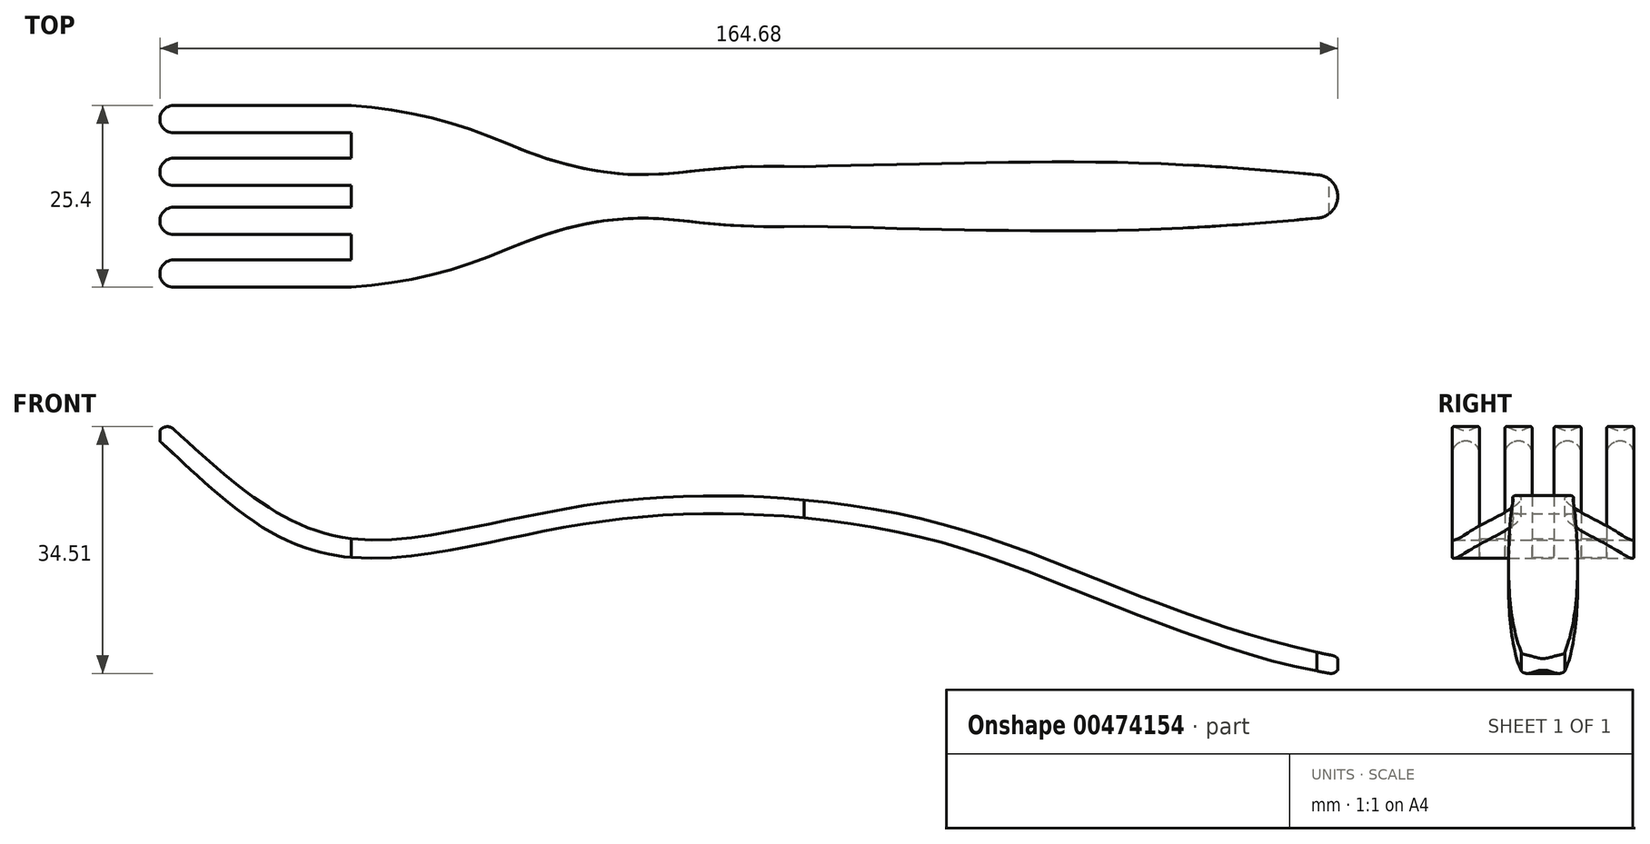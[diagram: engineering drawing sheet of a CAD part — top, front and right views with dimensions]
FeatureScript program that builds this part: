
annotation { "Feature Type Name" : "Feature", "Feature Type Description" : "" }
export const myFeature = defineFeature(function(context is Context, id is Id, definition is map)
    precondition{}
    {
        {
            var Q0;
            Q0=qCreatedBy(makeId("Front.planeOp"),FACE);
            var sketch = newSketch(context, id + "F0", { "sketchPlane" : qUnion([Q0])});
            skFitSpline(sketch, "E0", {"points": [v(0, 0) * mm, v(13.61, -11.16) * mm, v(28.58, -15.5) * mm, v(60.74, -10.24) * mm, v(97.9, -11.19) * mm, v(122.55, -18.4) * mm, v(162.04, -31.66) * mm], "startDerivative": vector(98.22, -90.14) * mm, "endDerivative": vector(217.26, -42.93) * mm});
            skFitSpline(sketch, "E1.0", {"points": [v(-1.72, -1.87) * mm, v(0.33, -3.75) * mm, v(4.54, -7.63) * mm, v(11.25, -12.95) * mm, v(17.27, -16.18) * mm, v(22.74, -17.67) * mm, v(26.46, -18.07) * mm, v(29.66, -18.05) * mm, v(32.14, -17.87) * mm, v(34.7, -17.57) * mm, v(38.22, -17.03) * mm, v(42.8, -16.14) * mm, v(48.55, -14.94) * mm, v(53.5, -13.95) * mm, v(57.51, -13.26) * mm, v(60.54, -12.8) * mm, v(63.59, -12.45) * mm, v(67.68, -12.09) * mm, v(72.82, -11.85) * mm, v(78.93, -11.86) * mm, v(84.9, -12.15) * mm, v(89.7, -12.6) * mm, v(93.36, -13.05) * mm, v(96.02, -13.44) * mm, v(98.57, -13.88) * mm, v(101.84, -14.5) * mm, v(105.73, -15.41) * mm, v(110.23, -16.69) * mm, v(114.74, -18.17) * mm, v(118.64, -19.6) * mm, v(121.92, -20.87) * mm, v(125.34, -22.22) * mm, v(129.84, -24.04) * mm, v(135.6, -26.3) * mm, v(141.68, -28.57) * mm, v(150.16, -31.43) * mm, v(156.9, -33.24) * mm, v(161.54, -34.16) * mm]});
            skArc(sketch, "E2", {"start": v(0, 0) * mm, "mid": v(-1.8, -0.08) * mm, "end": v(-1.72, -1.87) * mm});
            skArc(sketch, "E3", {"start": v(161.54, -34.16) * mm, "mid": v(163.03, -33.16) * mm, "end": v(162.04, -31.66) * mm});
            skSolve(sketch);
        }
        {
            var Q0;
            Q0 = qSketchRegion(id + "F0", true);
            extrude(context, id + "F1", {"entities" : qUnion([Q0]), "depth" : 25.4 * mm});
        }
        {
            var Q0;
            Q0=qCreatedBy(makeId("Top.planeOp"),FACE);
            var sketch = newSketch(context, id + "F2", { "sketchPlane" : qUnion([Q0])});
            skLineSegment(sketch, "E4.bottom", {"start": v(-6.25, 9.3) * mm, "end": v(172.92, 9.3) * mm});
            skLineSegment(sketch, "E4.top", {"start": v(-6.25, -34.7) * mm, "end": v(172.92, -34.7) * mm});
            skLineSegment(sketch, "E4.left", {"start": v(-6.25, 9.3) * mm, "end": v(-6.25, -34.7) * mm});
            skLineSegment(sketch, "E4.right", {"start": v(172.92, 9.3) * mm, "end": v(172.92, -34.7) * mm});
            skFitSpline(sketch, "E5", {"points": [v(0, 0) * mm, v(24.83, 0) * mm, v(41.72, -3.41) * mm, v(52.72, -7.58) * mm, v(65.82, -9.67) * mm, v(88.17, -8.53) * mm], "startDerivative": vector(74.86, 1.88) * mm, "endDerivative": vector(153.2, -5.47) * mm});
            skFitSpline(sketch, "E6", {"points": [v(88.17, -8.53) * mm, v(159.85, -9.67) * mm], "startDerivative": vector(101.81, 2.28) * mm, "endDerivative": vector(79.44, -7.5) * mm});
            skLineSegment(sketch, "E7", {"start": v(-6.25, -12.7) * mm, "end": v(172.92, -12.7) * mm, "construction": true});
            skFitSpline(sketch, "E8.MirrorCS", {"points": [v(88.17, -16.87) * mm, v(159.85, -15.73) * mm], "startDerivative": vector(101.81, -2.28) * mm, "endDerivative": vector(79.44, 7.5) * mm});
            skFitSpline(sketch, "E9.MirrorCS", {"points": [v(0, -25.4) * mm, v(24.83, -25.4) * mm, v(41.72, -21.99) * mm, v(52.72, -17.82) * mm, v(65.82, -15.73) * mm, v(88.17, -16.87) * mm], "startDerivative": vector(74.86, -1.88) * mm, "endDerivative": vector(153.2, 5.47) * mm});
            skArc(sketch, "E10", {"start": v(159.85, -15.73) * mm, "mid": v(162.77, -12.7) * mm, "end": v(159.85, -9.67) * mm});
            skLineSegment(sketch, "E11", {"start": v(24.83, -12.7) * mm, "end": v(0, -12.7) * mm});
            skLineSegment(sketch, "E12", {"start": v(0, -3.81) * mm, "end": v(24.83, -3.81) * mm});
            skLineSegment(sketch, "E13", {"start": v(24.83, -3.81) * mm, "end": v(24.83, -7.37) * mm});
            skPoint(sketch, "E14.orphan", {"position": v(24.83, 1.62) * mm});
            skLineSegment(sketch, "E15", {"start": v(24.83, 0) * mm, "end": v(0, 0) * mm});
            skArc(sketch, "E16", {"start": v(0, 0) * mm, "mid": v(-1.9, -1.9) * mm, "end": v(0, -3.8) * mm});
            skLineSegment(sketch, "E17", {"start": v(24.83, -5.59) * mm, "end": v(-4.53, -5.59) * mm, "construction": true});
            skLineSegment(sketch, "E18.MirrorCS", {"start": v(24.83, -7.37) * mm, "end": v(24.83, -3.8) * mm});
            skLineSegment(sketch, "E19.MirrorCS", {"start": v(0, -7.37) * mm, "end": v(24.83, -7.37) * mm});
            skArc(sketch, "E20.MirrorCS", {"start": v(0, -11.18) * mm, "mid": v(-1.9, -9.27) * mm, "end": v(0, -7.37) * mm});
            skLineSegment(sketch, "E21.MirrorCS", {"start": v(24.83, -11.18) * mm, "end": v(0, -11.18) * mm});
            skLineSegment(sketch, "E22", {"start": v(24.83, -11.18) * mm, "end": v(24.83, -12.7) * mm});
            skLineSegment(sketch, "E23.MirrorCS", {"start": v(24.83, -14.22) * mm, "end": v(24.83, -12.7) * mm});
            skLineSegment(sketch, "E24.MirrorCS", {"start": v(24.83, -14.22) * mm, "end": v(0, -14.22) * mm});
            skArc(sketch, "E25.MirrorCS", {"start": v(0, -14.22) * mm, "mid": v(-1.9, -16.13) * mm, "end": v(0, -18.03) * mm});
            skLineSegment(sketch, "E26.MirrorCS", {"start": v(0, -18.03) * mm, "end": v(24.83, -18.03) * mm});
            skLineSegment(sketch, "E27.MirrorCS", {"start": v(24.83, -21.59) * mm, "end": v(24.83, -18.03) * mm});
            skLineSegment(sketch, "E28.MirrorCS", {"start": v(0, -21.59) * mm, "end": v(24.83, -21.59) * mm});
            skLineSegment(sketch, "E29.MirrorCS", {"start": v(24.83, -25.4) * mm, "end": v(0, -25.4) * mm});
            skArc(sketch, "E30.MirrorCS", {"start": v(0, -25.4) * mm, "mid": v(-1.9, -23.5) * mm, "end": v(0, -21.6) * mm});
            skSolve(sketch);
        }
        {
            var Q0;
            Q0 = qSketchRegion(id + "F2", true);
            extrude(context, id + "F3", {"entities" : qUnion([Q0]), "operationType" : NewBodyOperationType.REMOVE, "oppositeDirection" : true, "depth" : 100.58 * mm, "hasSecondDirection" : true, "secondDirectionOppositeDirection" : false, "secondDirectionDepth" : 27.43 * mm});
        }
    });
